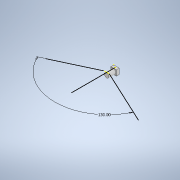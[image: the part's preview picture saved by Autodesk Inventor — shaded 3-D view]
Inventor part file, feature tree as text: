
AUTODESK INVENTOR PART (.ipt)
format: ipt  version: 2020 (Build 240168000, 168)  size: 130,560 bytes
history: native  units: in
note: dims shown in document units (in); Inventor stores cm internally (conversion verified against a paired STEP export)
features: sketch x5, extrude x3, projected_geometry x1
ambient origin geometry x8: Origin, YZ Plane, XZ Plane, XY Plane, X Axis, Y Axis, Z Axis, Center Point
bodies: Solid1 (feature_tree)
feature tree (9):
  extrude  "Extrusion1"  Depth=0.5689in
  sketch  "Sketch6"  dims[d2=0.2953in d3=0.0in d14=0.4724in]
  sketch  "Sketch7"  dims[d15=0.2953in d16=0.7087in d17=0.0in]
  extrude  "Extrusion4"  Depth=0.2953in
  extrude  "Extrusion5"  Depth=0.7087in TaperAngle=0.0deg
  sketch  "Sketch10"  dims[d19=0.0787in d20=0.7087in d21=0.0in d22=0.8933in]
  sketch  "Sketch1"  dims[d0=0.5689in d1=0.5689in]
  projected_geometry  "Projected Loop4"
  sketch  "Sketch8"  dims[d18=0.1969in]
